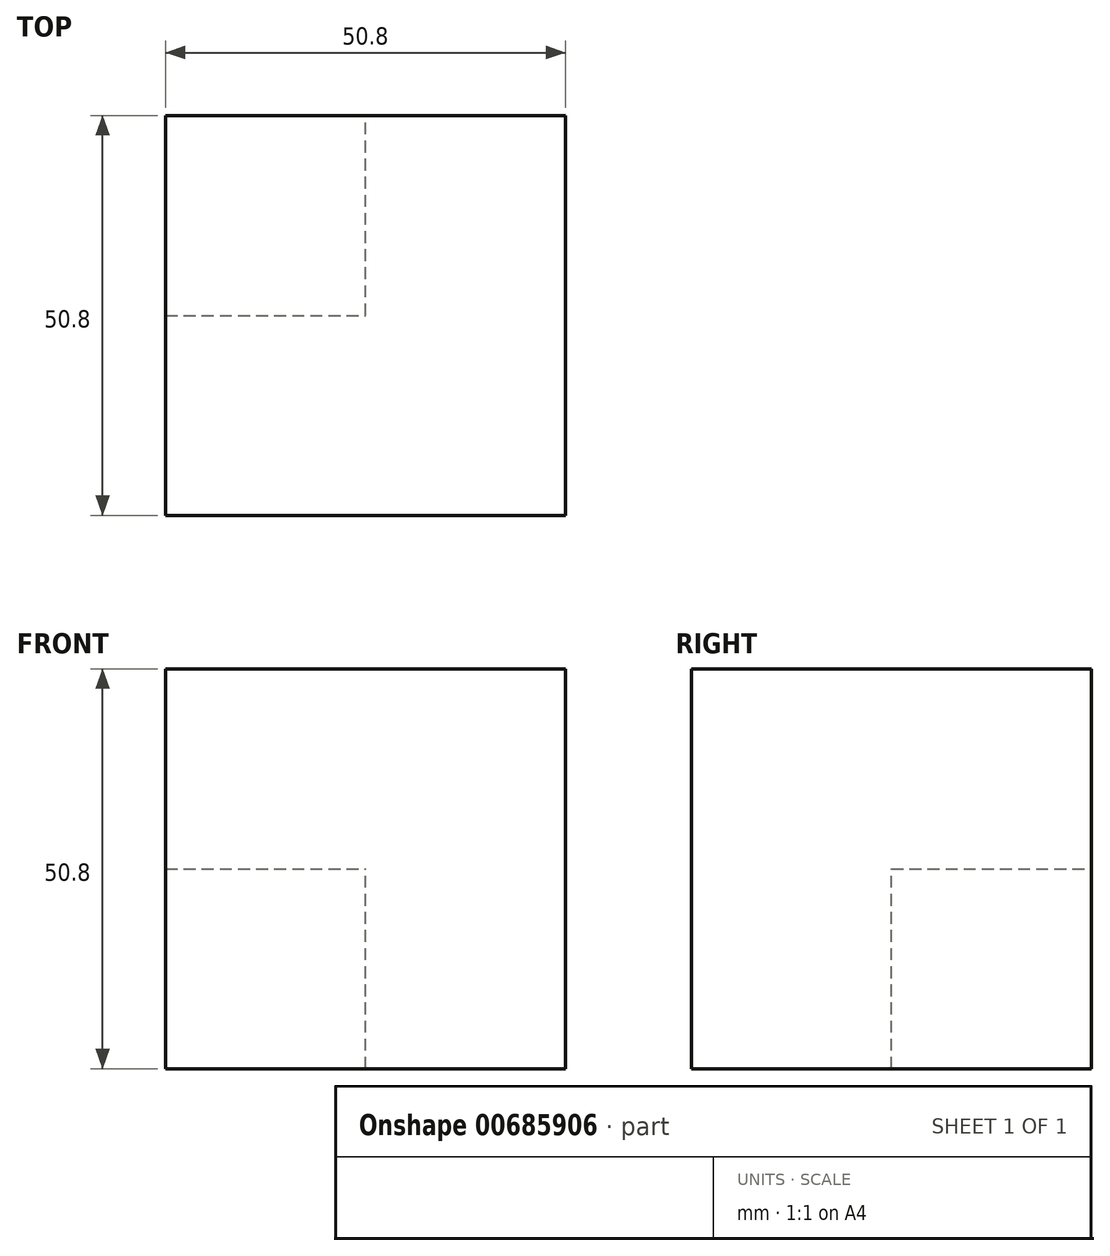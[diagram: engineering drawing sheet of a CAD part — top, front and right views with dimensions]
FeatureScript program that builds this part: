
annotation { "Feature Type Name" : "Feature", "Feature Type Description" : "" }
export const myFeature = defineFeature(function(context is Context, id is Id, definition is map)
    precondition{}
    {
        {
            var Q0;
            Q0=qCreatedBy(makeId("Front.planeOp"),FACE);
            var sketch = newSketch(context, id + "F0", { "sketchPlane" : qUnion([Q0])});
            skLineSegment(sketch, "E0.bottom", {"start": v(0, 0) * mm, "end": v(50.8, 0) * mm});
            skLineSegment(sketch, "E0.top", {"start": v(0, 50.8) * mm, "end": v(50.8, 50.8) * mm});
            skLineSegment(sketch, "E0.left", {"start": v(0, 0) * mm, "end": v(0, 50.8) * mm});
            skLineSegment(sketch, "E0.right", {"start": v(50.8, 0) * mm, "end": v(50.8, 50.8) * mm});
            skSolve(sketch);
        }
        {
            var Q0;
            Q0=makeQuery(id+"F0.imprint","IMPRINT",FACE,{"disambiguationData":[TD([[makeQuery(id+"F0.imprint","IMPRINT",EDGE,{"derivedFrom":sQuery(id+"F0.wireOp",EDGE,"E0.bottom")}),1.0]])]});
            extrude(context, id + "F1", {"entities" : qUnion([Q0]), "depth" : 50.8 * mm, "offsetDistance" : 25.4 * mm});
        }
        {
            var Q0;
            Q0=qCreatedBy(makeId("Front.planeOp"),FACE);
            var sketch = newSketch(context, id + "F2", { "sketchPlane" : qUnion([Q0])});
            skLineSegment(sketch, "E1.bottom", {"start": v(0, 0) * mm, "end": v(25.4, 0) * mm});
            skLineSegment(sketch, "E1.top", {"start": v(0, 25.4) * mm, "end": v(25.4, 25.4) * mm});
            skLineSegment(sketch, "E1.left", {"start": v(0, 0) * mm, "end": v(0, 25.4) * mm});
            skLineSegment(sketch, "E1.right", {"start": v(25.4, 0) * mm, "end": v(25.4, 25.4) * mm});
            skSolve(sketch);
        }
        {
            var Q0;
            Q0 = qSketchRegion(id + "F2", true);
            extrude(context, id + "F3", {"entities" : qUnion([Q0]), "operationType" : NewBodyOperationType.REMOVE, "depth" : 25.4 * mm, "offsetDistance" : 25.4 * mm});
        }
    });
